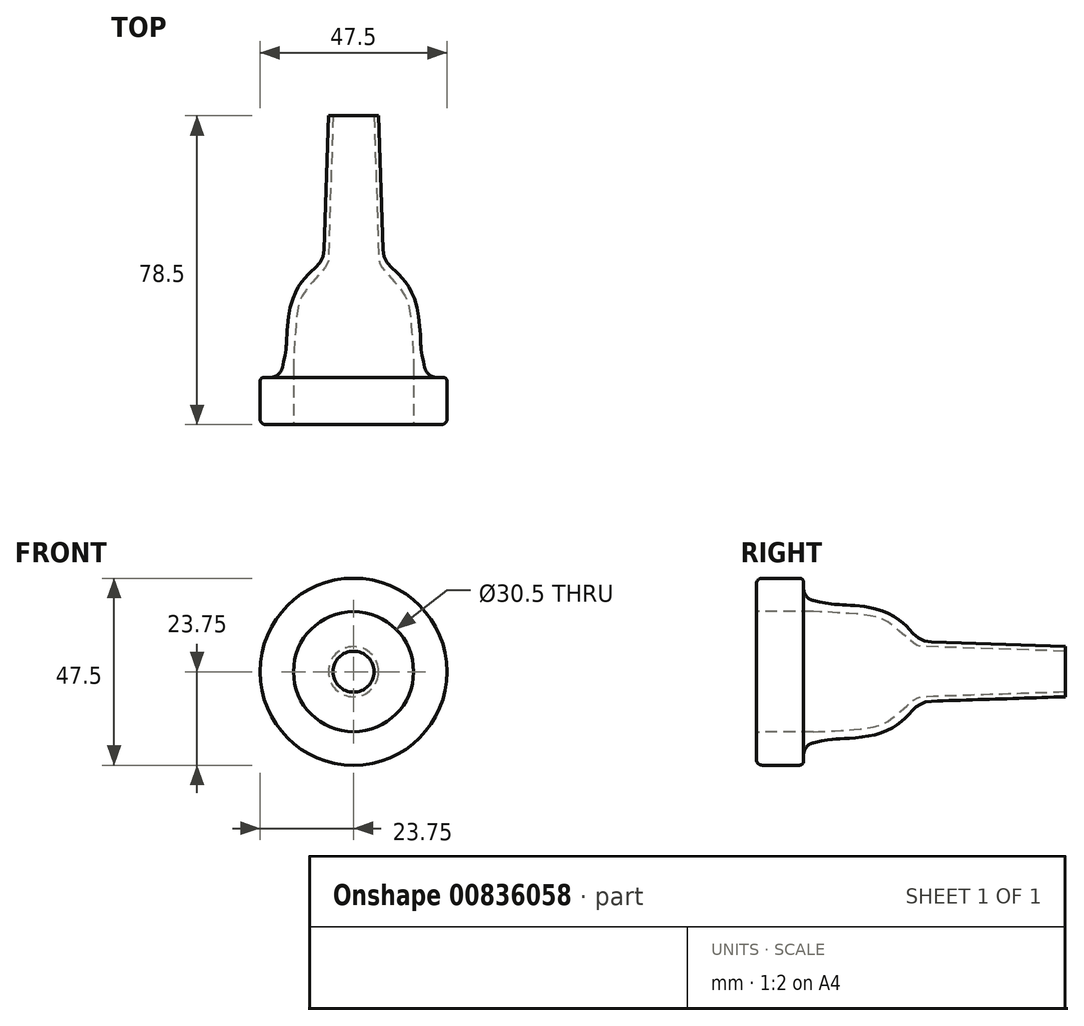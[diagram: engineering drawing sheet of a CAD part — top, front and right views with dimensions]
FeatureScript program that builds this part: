
annotation { "Feature Type Name" : "Feature", "Feature Type Description" : "" }
export const myFeature = defineFeature(function(context is Context, id is Id, definition is map)
    precondition{}
    {
        {
            var Q0;
            Q0=qCreatedBy(makeId("Top.planeOp"),FACE);
            var sketch = newSketch(context, id + "F0", { "sketchPlane" : qUnion([Q0])});
            skLineSegment(sketch, "E0", {"start": v(0, 0) * mm, "end": v(0, 90) * mm, "construction": true});
            skLineSegment(sketch, "E1", {"start": v(23.75, 1.5) * mm, "end": v(23.75, 11) * mm});
            skLineSegment(sketch, "E2", {"start": v(16, 0) * mm, "end": v(22.25, 0) * mm});
            skLineSegment(sketch, "E3", {"start": v(21.25, 12) * mm, "end": v(22.75, 12) * mm});
            skArc(sketch, "E4.filletArc", {"start": v(18.09, 14.5) * mm, "mid": v(19.23, 12.7) * mm, "end": v(21.25, 12) * mm});
            skPoint(sketch, "E5.visualSharp", {"position": v(23.75, 12) * mm});
            skArc(sketch, "E5.filletArc", {"start": v(23.75, 11) * mm, "mid": v(23.46, 11.7) * mm, "end": v(22.75, 12) * mm});
            skPoint(sketch, "E6.visualSharp", {"position": v(23.75, 0) * mm});
            skArc(sketch, "E6.filletArc", {"start": v(22.25, 0) * mm, "mid": v(23.31, 0.44) * mm, "end": v(23.75, 1.5) * mm});
            skLineSegment(sketch, "E7", {"start": v(15.25, 0.75) * mm, "end": v(15.25, 14.5) * mm});
            skPoint(sketch, "E8.visualSharp", {"position": v(15.25, 0) * mm});
            skArc(sketch, "E8.filletArc", {"start": v(15.25, 0.75) * mm, "mid": v(15.47, 0.22) * mm, "end": v(16, 0) * mm});
            skLineSegment(sketch, "E9", {"start": v(7.5, 44.5) * mm, "end": v(6.38, 78.5) * mm});
            skLineSegment(sketch, "E10", {"start": v(6.38, 78.5) * mm, "end": v(5.2, 78.46) * mm});
            skLineSegment(sketch, "E11", {"start": v(5.2, 78.46) * mm, "end": v(6.41, 41.75) * mm});
            skFitSpline(sketch, "E12", {"points": [v(7.5, 44.5) * mm, v(11.18, 38.5) * mm, v(15.65, 31.38) * mm, v(17, 21.74) * mm, v(18.09, 14.5) * mm], "startDerivative": vector(1.36, -41.04) * mm, "endDerivative": vector(13.13, -55.38) * mm});
            skFitSpline(sketch, "E13", {"points": [v(15.25, 14.5) * mm, v(14.9, 21.74) * mm, v(13.6, 31.38) * mm, v(11.18, 35.3) * mm, v(8.47, 38.5) * mm, v(6.41, 41.75) * mm], "startDerivative": vector(0, 30.07) * mm, "endDerivative": vector(-0.6, 18.06) * mm});
            skLineSegment(sketch, "E14", {"start": v(0, 0) * mm, "end": v(0, 45) * mm});
            skSolve(sketch);
        }
        {
            var Q0;
            Q0=makeQuery(id+"F0.imprint","IMPRINT",FACE,{"disambiguationData":[TD([[makeQuery(id+"F0.imprint","IMPRINT",EDGE,{"derivedFrom":sQuery(id+"F0.wireOp",EDGE,"E1")}),1.0]])]});
            var Q1;
            Q1=sQuery(id+"F0.wireOp",EDGE,"E0");
            revolve(context, id + "F1", {"surfaceOperationType" : NewSurfaceOperationType.NEW, "entities" : qUnion([Q0]), "axis" : qUnion([Q1]), "revolveType" : RevolveType.FULL});
        }
    });
